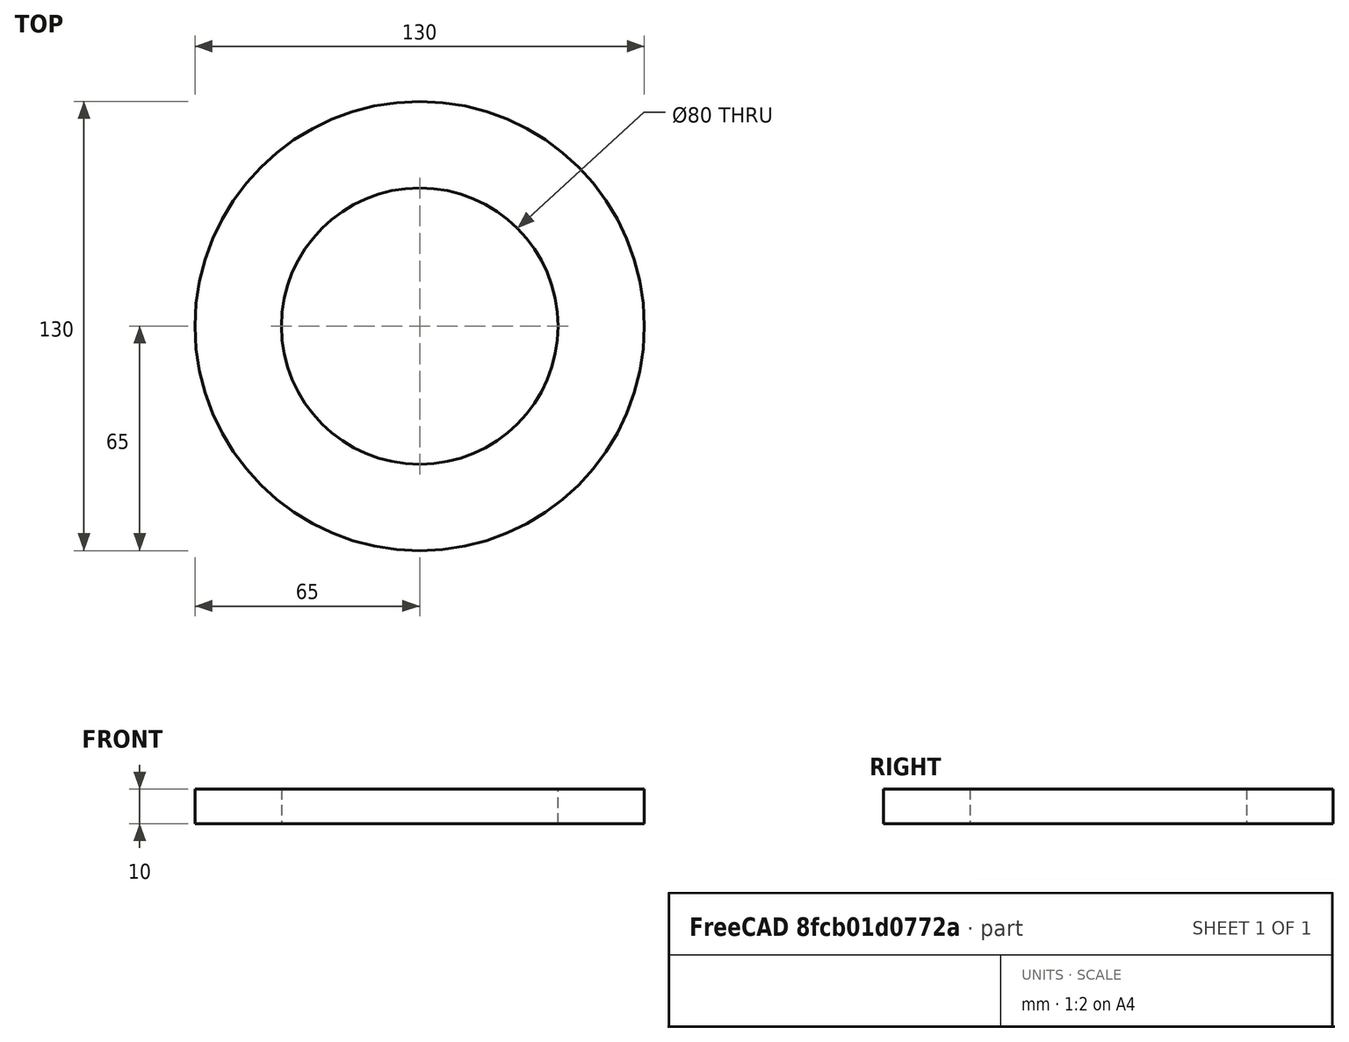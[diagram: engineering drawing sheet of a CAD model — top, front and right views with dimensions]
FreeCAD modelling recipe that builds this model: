
FCSTD DOCUMENT  (FreeCAD 0.19R24276 (Git))
Label: Katushka_strips_1
License: All rights reserved
LicenseURL: http://en.wikipedia.org/wiki/All_rights_reserved
objects: Sketcher::SketchObject×1, PartDesign::Pad×1, PartDesign::Body×1
note: 4 computed .brp shape members not serialized (recipe doc carries the construction recipe); baked Part::Feature solids carry a one-line shape summary decoded from their .brp

FEATURE [Sketcher::SketchObject] Sketch
  FullyConstrained = true
  MapMode = 5
  Support = -> [XY_Plane]
  sketch-geometry (2):
    g0: Circle CenterX=0 CenterY=0 CenterZ=0 NormalX=0 NormalY=0 NormalZ=1 AngleXU=0 Radius=40
    g1: Circle CenterX=0 CenterY=0 CenterZ=0 NormalX=0 NormalY=0 NormalZ=1 AngleXU=0 Radius=65
  constraints (4):
    c: Coincident(g0,g-1)
    c: Coincident(g1,g0)
    c: Diameter(g0) = 80
    c: Diameter(g1) = 130
FEATURE [PartDesign::Pad] Pad
  Direction = (1,1,1)
  Length = 10
  Length2 = 100
  Profile = -> Sketch
  Type = 0
FEATURE [PartDesign::Body] Body
  Group = -> [Sketch,Pad]
  Origin = -> Origin
  Tip = -> Pad
